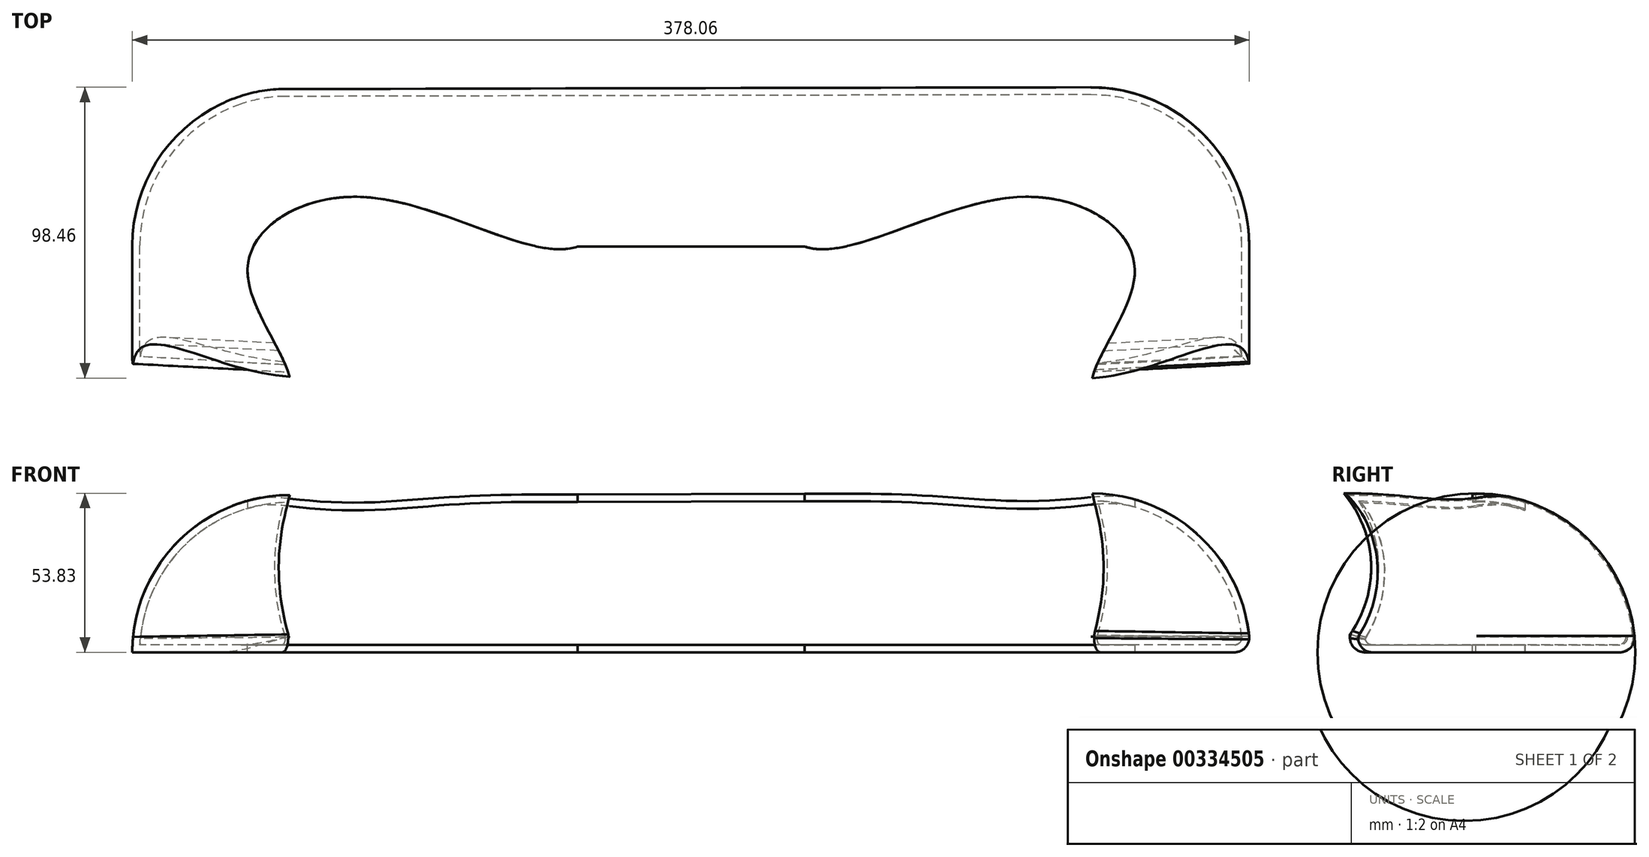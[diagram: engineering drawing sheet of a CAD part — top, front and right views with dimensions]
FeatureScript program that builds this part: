
annotation { "Feature Type Name" : "Feature", "Feature Type Description" : "" }
export const myFeature = defineFeature(function(context is Context, id is Id, definition is map)
    precondition{}
    {
        {
            var Q0;
            Q0=qCreatedBy(makeId("Front.planeOp"),FACE);
            cPlane(context, id + "F0", {"entities" : qUnion([Q0]), "cplaneType" : CPlaneType.OFFSET, "offset" : 60.04 * mm, "width" : 150 * mm, "height" : 150 * mm});
        }
        {
            var Q0;
            Q0=qCreatedBy(id+"F0.planeOp",FACE);
            var sketch = newSketch(context, id + "F1", { "sketchPlane" : qUnion([Q0])});
            skLineSegment(sketch, "E0", {"start": v(189.16, 0) * mm, "end": v(-189.16, 0) * mm});
            skArc(sketch, "E1", {"start": v(-135.93, 53.23) * mm, "mid": v(-173.57, 37.64) * mm, "end": v(-189.16, 0) * mm});
            skArc(sketch, "E2", {"start": v(189.16, 0) * mm, "mid": v(173.4, 38.06) * mm, "end": v(135.33, 53.83) * mm});
            skLineSegment(sketch, "E3", {"start": v(-135.93, 53.23) * mm, "end": v(135.33, 53.83) * mm});
            skSolve(sketch);
        }
        {
            var Q0;
            Q0=qSketchRegion(id+"F1",true);
            var Q1;
            Q1=sQuery(id+"F1.wireOp",EDGE,"E0");
            revolve(context, id + "F2", {"entities" : qUnion([Q0]), "axis" : qUnion([Q1]), "revolveType" : RevolveType.ONE_DIRECTION, "angle" : 90 * degree});
        }
        {
            var Q0;
            Q0=makeQuery(id+"F2.opRevolve","CAP_FACE",FACE,{"disambiguationData":[OSD([sQuery(id+"F1.wireOp",EDGE,"E0"),sQuery(id+"F1.wireOp",EDGE,"E1"),sQuery(id+"F1.wireOp",EDGE,"E2"),sQuery(id+"F1.wireOp",EDGE,"E3")])],"isStart":true});
            extrude(context, id + "F3", {"entities" : qUnion([Q0]), "operationType" : NewBodyOperationType.ADD, "depth" : 50 * mm});
        }
        {
            var Q0;
            Q0=qCreatedBy(makeId("Top.planeOp"),FACE);
            var sketch = newSketch(context, id + "F4", { "sketchPlane" : qUnion([Q0])});
            skFitSpline(sketch, "E4", {"points": [v(135.33, -110.04) * mm, v(150.16, -68.16) * mm, v(111.06, -43.62) * mm, v(38.43, -60.39) * mm], "startDerivative": vector(-14.92, 102.87) * mm, "endDerivative": vector(-119.7, 42.24) * mm});
            skLineSegment(sketch, "E5", {"start": v(38.43, -60.39) * mm, "end": v(0, -60.39) * mm});
            skFitSpline(sketch, "E6.MirrorCS", {"points": [v(-135.33, -110.04) * mm, v(-150.16, -68.16) * mm, v(-111.06, -43.62) * mm, v(-38.43, -60.39) * mm], "startDerivative": vector(14.92, 102.87) * mm, "endDerivative": vector(119.7, 42.24) * mm});
            skLineSegment(sketch, "E7.MirrorCS", {"start": v(-38.43, -60.39) * mm, "end": v(0, -60.39) * mm});
            skLineSegment(sketch, "E8", {"start": v(-135.33, -110.04) * mm, "end": v(135.33, -110.04) * mm});
            skSolve(sketch);
        }
        {
            var Q0;
            Q0=qSketchRegion(id+"F4",true);
            extrude(context, id + "F5", {"entities" : qUnion([Q0]), "operationType" : NewBodyOperationType.REMOVE, "depth" : 60 * mm});
        }
        {
            var Q0;
            Q0=qCreatedBy(makeId("Right.planeOp"),FACE);
            var sketch = newSketch(context, id + "F6", { "sketchPlane" : qUnion([Q0])});
            skArc(sketch, "E9", {"start": v(-108.35, 10.69) * mm, "mid": v(-103, 29.65) * mm, "end": v(-109.57, 48.22) * mm});
            skPoint(sketch, "E10.visualSharp", {"position": v(-110.04, 48.83) * mm});
            skArc(sketch, "E10.filletArc", {"start": v(-109.95, 48.76) * mm, "mid": v(-109.76, 48.5) * mm, "end": v(-109.57, 48.22) * mm});
            skPoint(sketch, "E11.visualSharp", {"position": v(-110.04, 8.36) * mm});
            skArc(sketch, "E11.filletArc", {"start": v(-108.35, 10.69) * mm, "mid": v(-109.61, 7.97) * mm, "end": v(-110, 5) * mm});
            skLineSegment(sketch, "E12", {"start": v(-110, 5) * mm, "end": v(-109.95, 48.76) * mm});
            skSolve(sketch);
        }
        {
            var Q0;
            Q0=qSketchRegion(id+"F6",true);
            extrude(context, id + "F7", {"entities" : qUnion([Q0]), "operationType" : NewBodyOperationType.REMOVE, "endBound" : BoundingType.SYMMETRIC, "depth" : 400 * mm, "hasDraft" : true, "draftAngle" : 3 * degree, "hasSecondDirection" : true, "secondDirectionOppositeDirection" : true, "secondDirectionDepth" : 25 * mm});
        }
        {
            var Q0;
            {var subQ0=sQuery(id+"F6.wireOp",EDGE,"E12");var subQ1=sQuery(id+"F6.wireOp",EDGE,"E11.filletArc");Q0=makeQuery(id+"F7.boolean.opBoolean","INTERSECT",EDGE,{"derivedFrom":[makeQuery(id+"F7.*.split.splitOp","SPLIT",FACE,{"derivedFrom":makeQuery(id+"F7.opExtrude","SWEPT_FACE",FACE,{"disambiguationData":[OSD([sQuery(id+"F6.wireOp",EDGE,"E9")])]})}),makeQuery(id+"F7.*.split.splitOp","SPLIT",FACE,{"derivedFrom":makeQuery(id+"F7.opExtrude","SWEPT_FACE",FACE,{"disambiguationData":[OSD([subQ0]),TDD([makeQuery(id+"F6.imprint","IMPRINT",EDGE,{"disambiguationData":[TD([[makeQuery(id+"F6.imprint","INTERSECT",VERTEX,{"disambiguationData":[OD(0.0)],"derivedFrom":[subQ1,subQ0]}),-1.0]])],"derivedFrom":subQ0})])]})})]});}
            var Q1;
            {var subQ0=sQuery(id+"F6.wireOp",EDGE,"E12");var subQ1=sQuery(id+"F6.wireOp",EDGE,"E11.filletArc");var subQ2=sQuery(id+"F1.wireOp",EDGE,"E0");Q1=makeQuery(id+"F7.boolean.opBoolean","INTERSECT",EDGE,{"derivedFrom":[makeQuery(id+"F3.boolean.opBoolean","MERGE",FACE,{"derivedFrom":[makeQuery(id+"F2.opRevolve","CAP_FACE",FACE,{"disambiguationData":[OSD([subQ2,sQuery(id+"F1.wireOp",EDGE,"E1"),sQuery(id+"F1.wireOp",EDGE,"E2"),sQuery(id+"F1.wireOp",EDGE,"E3")])],"isStart":false}),makeQuery(id+"F3.opExtrude","SWEPT_FACE",FACE,{"disambiguationData":[OSD([subQ2])]})]}),makeQuery(id+"F7.*.split.splitOp","SPLIT",FACE,{"derivedFrom":makeQuery(id+"F7.opExtrude","SWEPT_FACE",FACE,{"disambiguationData":[OSD([subQ0]),TDD([makeQuery(id+"F6.imprint","IMPRINT",EDGE,{"disambiguationData":[TD([[makeQuery(id+"F6.imprint","INTERSECT",VERTEX,{"disambiguationData":[OD(0.0)],"derivedFrom":[subQ1,subQ0]}),-1.0]])],"derivedFrom":subQ0})])]})})]});}
            var Q2;
            {var subQ0=sQuery(id+"F6.wireOp",EDGE,"E12");var subQ1=sQuery(id+"F6.wireOp",EDGE,"E11.filletArc");var subQ2=sQuery(id+"F1.wireOp",EDGE,"E0");Q2=makeQuery(id+"F7.boolean.opBoolean","INTERSECT",EDGE,{"derivedFrom":[makeQuery(id+"F3.boolean.opBoolean","MERGE",FACE,{"derivedFrom":[makeQuery(id+"F2.opRevolve","CAP_FACE",FACE,{"disambiguationData":[OSD([subQ2,sQuery(id+"F1.wireOp",EDGE,"E1"),sQuery(id+"F1.wireOp",EDGE,"E2"),sQuery(id+"F1.wireOp",EDGE,"E3")])],"isStart":false}),makeQuery(id+"F3.opExtrude","SWEPT_FACE",FACE,{"disambiguationData":[OSD([subQ2])]})]}),makeQuery(id+"F7.*.split.splitOp","SPLIT",FACE,{"derivedFrom":makeQuery(id+"F7.opExtrude","SWEPT_FACE",FACE,{"disambiguationData":[OSD([subQ0]),TDD([makeQuery(id+"F6.imprint","IMPRINT",EDGE,{"disambiguationData":[TD([[makeQuery(id+"F6.imprint","INTERSECT",VERTEX,{"disambiguationData":[OD(0.0)],"derivedFrom":[subQ1,subQ0]}),-1.0]])],"derivedFrom":subQ0})])]}),"isFromBackBody":true})]});}
            var Q3;
            Q3=makeQuery(id+"F2.opRevolve","CAP_EDGE",EDGE,{"disambiguationData":[OSD([sQuery(id+"F1.wireOp",EDGE,"E2")])],"isStart":false});
            fillet(context, id + "F8", {"entities" : qUnion([Q0, Q1, Q2, Q3]), "radius" : 5 * mm, "tangentPropagation" : true, "allowEdgeOverflow" : false});
        }
        {
            var Q0;
            Q0=makeQuery(id+"F5.boolean.opBoolean","COPY",FACE,{"derivedFrom":makeQuery(id+"F5.opExtrude","SWEPT_FACE",FACE,{"disambiguationData":[OSD([sQuery(id+"F4.wireOp",EDGE,"E5"),sQuery(id+"F4.wireOp",EDGE,"E7.MirrorCS")])]})});
            var Q1;
            Q1=makeQuery(id+"F5.boolean.opBoolean","COPY",FACE,{"derivedFrom":makeQuery(id+"F5.opExtrude","SWEPT_FACE",FACE,{"disambiguationData":[OSD([sQuery(id+"F4.wireOp",EDGE,"E6.MirrorCS")])]})});
            var Q2;
            Q2=makeQuery(id+"F5.boolean.opBoolean","COPY",FACE,{"derivedFrom":makeQuery(id+"F5.opExtrude","SWEPT_FACE",FACE,{"disambiguationData":[OSD([sQuery(id+"F4.wireOp",EDGE,"E4")])]})});
            shell(context, id + "F9", {"entities" : qUnion([Q0, Q1, Q2]), "thickness" : 2.5 * mm});
        }
    });
